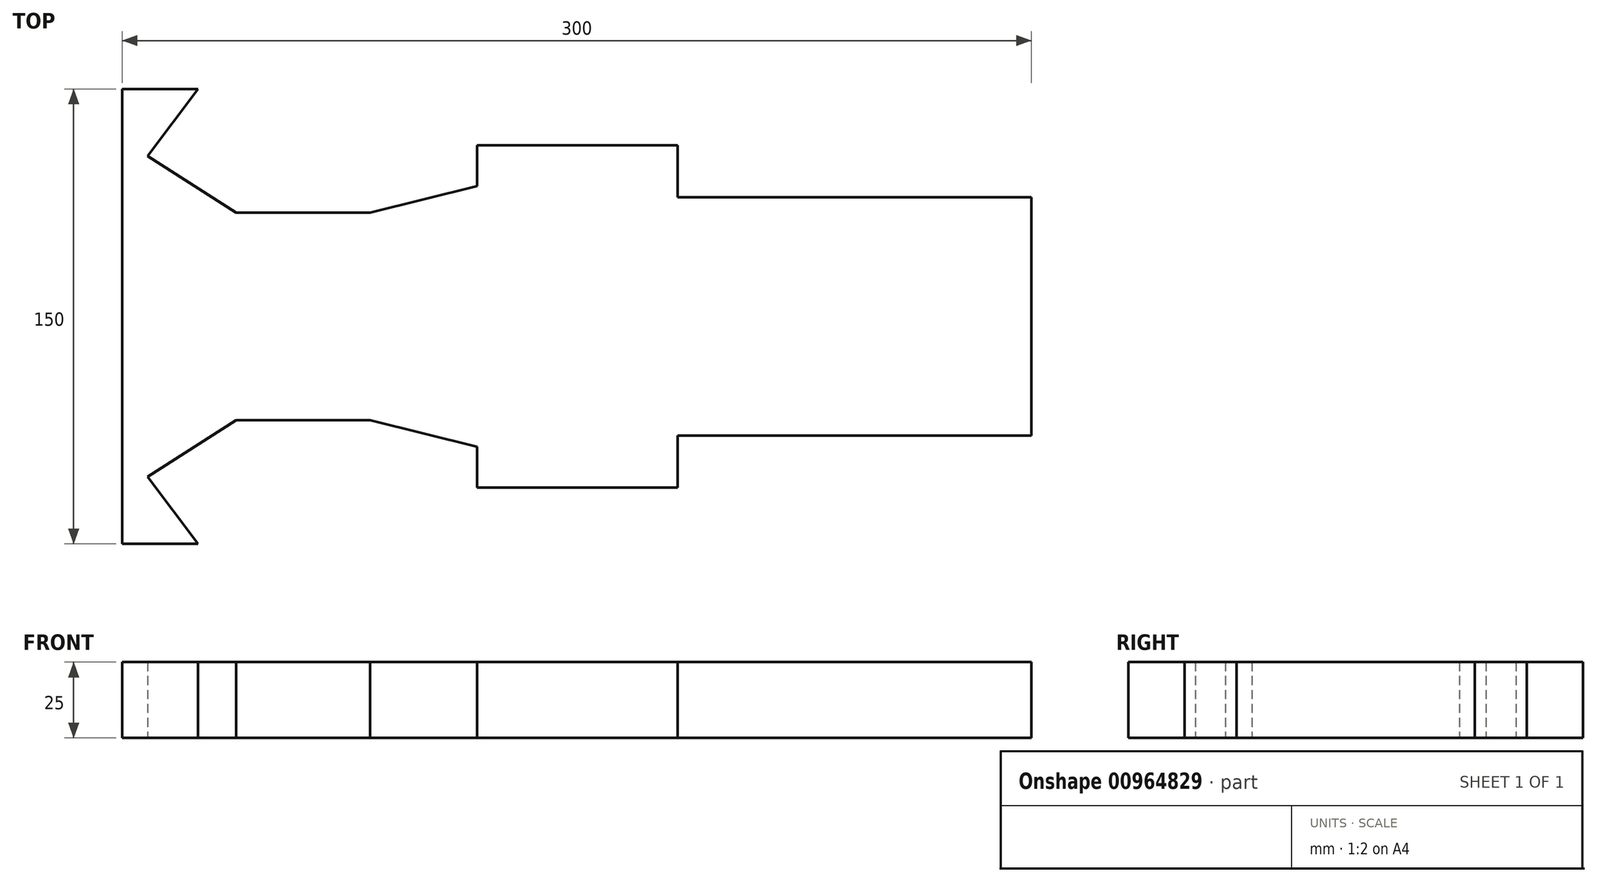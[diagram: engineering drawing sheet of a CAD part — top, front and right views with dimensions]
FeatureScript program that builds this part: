
annotation { "Feature Type Name" : "Feature", "Feature Type Description" : "" }
export const myFeature = defineFeature(function(context is Context, id is Id, definition is map)
    precondition{}
    {
        {
            var Q0;
            Q0=qCreatedBy(makeId("Top.planeOp"),FACE);
            var sketch = newSketch(context, id + "F0", { "sketchPlane" : qUnion([Q0])});
            skLineSegment(sketch, "E0.bottom", {"start": v(-145.05, 70.27) * mm, "end": v(154.95, 70.27) * mm});
            skLineSegment(sketch, "E0.top", {"start": v(-145.05, -79.73) * mm, "end": v(154.95, -79.73) * mm});
            skLineSegment(sketch, "E0.left", {"start": v(-145.05, 70.27) * mm, "end": v(-145.05, -79.73) * mm});
            skLineSegment(sketch, "E0.right", {"start": v(154.95, 70.27) * mm, "end": v(154.95, -79.73) * mm});
            skLineSegment(sketch, "E1", {"start": v(-145.05, -4.73) * mm, "end": v(208.08, -4.73) * mm});
            skLineSegment(sketch, "E2", {"start": v(-120, 70.27) * mm, "end": v(-136.6, 48.13) * mm});
            skLineSegment(sketch, "E3", {"start": v(-136.6, 48.13) * mm, "end": v(-107.37, 29.45) * mm});
            skLineSegment(sketch, "E4", {"start": v(-107.37, 29.45) * mm, "end": v(-63.23, 29.45) * mm});
            skLineSegment(sketch, "E5", {"start": v(-63.23, 29.45) * mm, "end": v(-27.87, 38.26) * mm});
            skLineSegment(sketch, "E6", {"start": v(-27.87, 38.26) * mm, "end": v(-27.87, 51.68) * mm});
            skLineSegment(sketch, "E7", {"start": v(-27.87, 51.68) * mm, "end": v(38.24, 51.68) * mm});
            skLineSegment(sketch, "E8", {"start": v(38.24, 51.68) * mm, "end": v(38.24, 34.56) * mm});
            skLineSegment(sketch, "E9", {"start": v(38.24, 34.56) * mm, "end": v(154.95, 34.56) * mm});
            skLineSegment(sketch, "E10", {"start": v(-120, -79.73) * mm, "end": v(-136.6, -57.6) * mm});
            skLineSegment(sketch, "E11", {"start": v(-136.6, -57.6) * mm, "end": v(-107.37, -38.9) * mm});
            skLineSegment(sketch, "E12", {"start": v(-107.37, -38.9) * mm, "end": v(-63.23, -38.9) * mm});
            skLineSegment(sketch, "E13", {"start": v(-63.23, -38.9) * mm, "end": v(-27.87, -47.72) * mm});
            skLineSegment(sketch, "E14", {"start": v(-27.87, -47.72) * mm, "end": v(-27.87, -61.14) * mm});
            skLineSegment(sketch, "E15", {"start": v(-27.87, -61.14) * mm, "end": v(38.24, -61.14) * mm});
            skLineSegment(sketch, "E16", {"start": v(38.24, -61.14) * mm, "end": v(38.24, -44.01) * mm});
            skLineSegment(sketch, "E17", {"start": v(38.24, -44.01) * mm, "end": v(154.95, -44.01) * mm});
            skSolve(sketch);
        }
        {
            var Q0;
            {var subQ0=sQuery(id+"F0.wireOp",EDGE,"E2");Q0=makeQuery(id+"F0.imprint","IMPRINT",FACE,{"disambiguationData":[TD([[makeQuery(id+"F0.imprint","IMPRINT",EDGE,{"derivedFrom":subQ0}),-1.0]])]});}
            var Q1;
            {var subQ3=sQuery(id+"F0.wireOp",EDGE,"E10");Q1=makeQuery(id+"F0.imprint","IMPRINT",FACE,{"disambiguationData":[TD([[makeQuery(id+"F0.imprint","IMPRINT",EDGE,{"derivedFrom":subQ3}),1.0]])]});}
            extrude(context, id + "F1", {"entities" : qUnion([Q0, Q1]), "depth" : 25 * mm, "offsetDistance" : 25 * mm});
        }
    });
